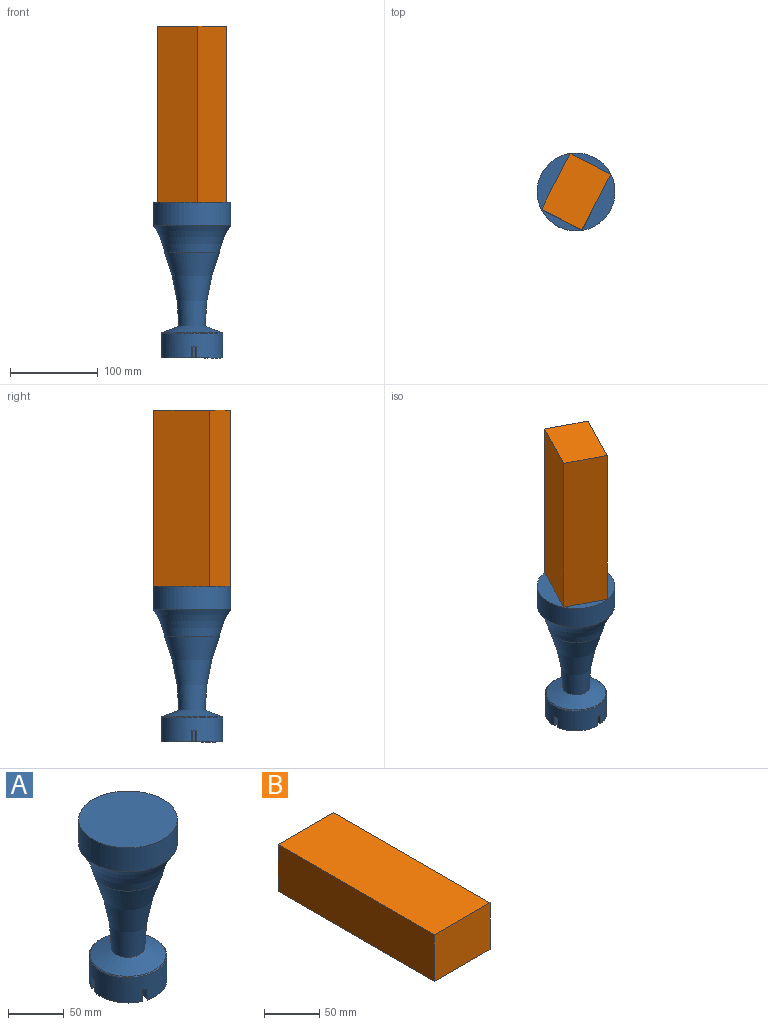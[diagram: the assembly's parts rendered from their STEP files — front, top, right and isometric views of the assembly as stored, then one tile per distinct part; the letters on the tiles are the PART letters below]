
ASSEMBLY  parts=2 mates=1
PART A: 25 faces, bbox 180x180x201.7 mm
  f0: cylinder r=34.95mm len=69.9mm, axis (0,0,-1), area 5816.1mm2, adj f1,f2,f3,f10,f12,f13,f14,f15
  f1: plane 41.06x24.76mm, normal (0,0,-1), area 409.5mm2, adj f0,f4,f15,f22
  f2: plane 41.06x24.76mm, normal (0,0,-1), area 409.5mm2, adj f0,f4,f12,f19
  f3: plane 41.06x24.76mm, normal (0,0,-1), area 409.5mm2, adj f0,f4,f16,f18
  f4: cylinder r=25.4mm len=50.8mm, axis (0,0,-1), area 3861.4mm2, adj f1,f2,f3,f10,f11,f12,f13,f14
  f5: plane 88.9x88.9mm, normal (0,0,1), area 6207.2mm2, adj f6
  f6: cylinder r=44.45mm len=88.9mm, axis (0,0,-1), area 7373.4mm2, adj f5,f7
  f7: torus R=106.28mm, axis (0,0,-1), area 7753.2mm2, adj f6,f8
  f8: torus R=249.99mm, axis (0,0,-1), area 11163.4mm2, adj f7,f9
  f9: cone r=34.95mm half-angle=68.8deg, axis (0,0,-1), area 3170.7mm2, adj f8,f24
  f10: plane 41.06x24.76mm, normal (0,0,-1), area 409.5mm2, adj f0,f4,f13,f21
  f11: plane 50.8x50.8mm, normal (0,0,-1), area 2026.8mm2, adj f4
  f12: plane 12.7x8.75mm, normal (-0.4,-0.92,0), area 121.3mm2, adj f0,f2,f4,f14
  f13: plane 12.7x9.24mm, normal (0.25,0.97,0), area 121.3mm2, adj f0,f4,f10,f14
  f14: plane 10.5x7.4mm, normal (0,0,-1), area 43.3mm2, adj f0,f4,f12,f13
  f15: plane 12.7x8.75mm, normal (0.4,0.92,0), area 121.3mm2, adj f0,f1,f4,f17
  f16: plane 12.7x9.24mm, normal (-0.25,-0.97,0), area 121.3mm2, adj f0,f3,f4,f17
  f17: plane 10.5x7.4mm, normal (0,0,-1), area 43.3mm2, adj f0,f4,f15,f16
  f18: plane 12.7x8.75mm, normal (-0.92,0.4,0), area 121.3mm2, adj f0,f3,f4,f20
  f19: plane 12.7x9.24mm, normal (0.97,-0.25,0), area 121.3mm2, adj f0,f2,f4,f20
  f20: plane 10.5x7.4mm, normal (0,0,-1), area 43.3mm2, adj f0,f4,f18,f19
  f21: plane 12.7x8.75mm, normal (0.92,-0.4,0), area 121.3mm2, adj f0,f4,f10,f23
  f22: plane 12.7x9.24mm, normal (-0.97,0.25,0), area 121.3mm2, adj f0,f1,f4,f23
  f23: plane 10.5x7.4mm, normal (0,0,-1), area 43.3mm2, adj f0,f4,f21,f22
  f24: torus R=33.68mm, axis (0,0,1), area 332.1mm2, adj f0,f9
PART B: 6 faces, bbox 71.4x200.8x51.9 mm
  f0: plane 200.78x51.86mm, normal (-1,0,0), area 10412mm2, adj f1,f3,f4,f5
  f1: plane 200.78x71.36mm, normal (0,0,-1), area 14328.3mm2, adj f0,f2,f4,f5
  f2: plane 200.78x51.86mm, normal (1,0,0), area 10412mm2, adj f1,f3,f4,f5
  f3: plane 200.78x71.36mm, normal (0,0,1), area 14328.3mm2, adj f0,f2,f4,f5
  f4: plane 71.36x51.86mm, normal (0,-1,0), area 3700.7mm2, adj f0,f1,f2,f3
  f5: plane 71.36x51.86mm, normal (0,1,0), area 3700.7mm2, adj f0,f1,f2,f3
PLACE A rot(axis=(0,0,-1),66.8deg) t=(515.13,145.98,0)mm
PLACE B rot(axis=(-0.4,0.65,-0.65),136.8deg) t=(321.95,-277.48,0)mm fixed
MATE revolute B.f5 <-> A.f7  axis (0,0,-1) through (328.68,-321.07,0)mm
